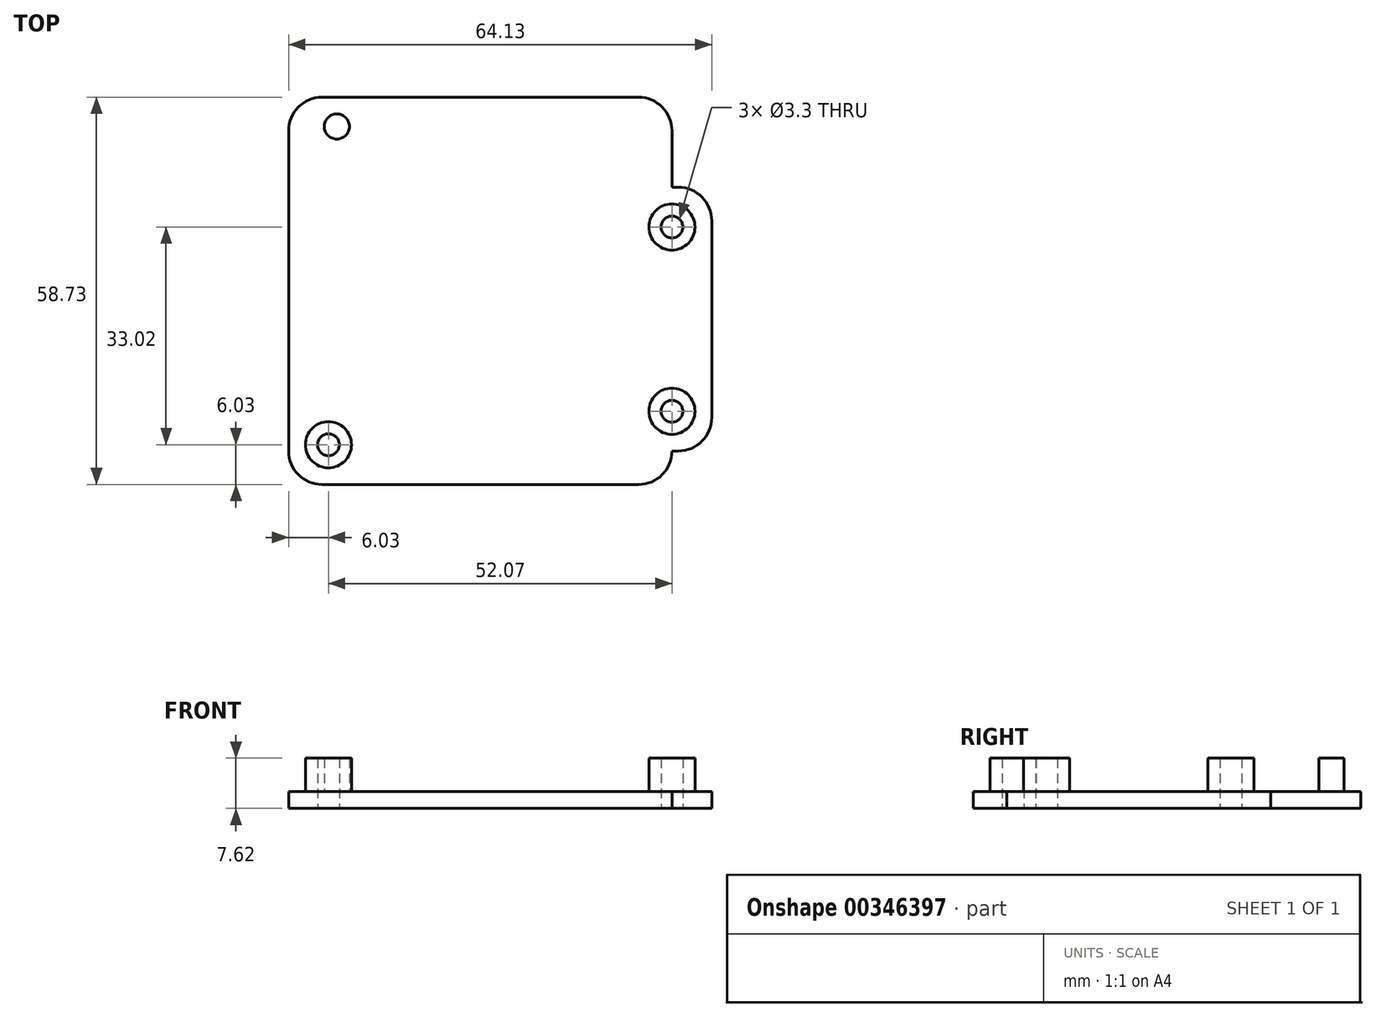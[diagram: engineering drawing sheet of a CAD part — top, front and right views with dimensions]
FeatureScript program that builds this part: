
annotation { "Feature Type Name" : "Feature", "Feature Type Description" : "" }
export const myFeature = defineFeature(function(context is Context, id is Id, definition is map)
    precondition{}
    {
        {
            var Q0;
            Q0=qCreatedBy(makeId("Top.planeOp"),FACE);
            var sketch = newSketch(context, id + "F0", { "sketchPlane" : qUnion([Q0])});
            skPoint(sketch, "E0.middle", {"position": v(0, 0) * mm});
            skLineSegment(sketch, "E1.bottom", {"start": v(25.4, -24.13) * mm, "end": v(-25.4, -24.13) * mm});
            skLineSegment(sketch, "E1.top", {"start": v(25.4, 24.13) * mm, "end": v(-25.4, 24.13) * mm});
            skLineSegment(sketch, "E1.left", {"start": v(25.4, -24.13) * mm, "end": v(25.4, 24.13) * mm});
            skLineSegment(sketch, "E1.right", {"start": v(-25.4, -24.13) * mm, "end": v(-25.4, 24.13) * mm});
            skLineSegment(sketch, "E2", {"start": v(-25.4, 8.9) * mm, "end": v(25.4, 8.9) * mm});
            skLineSegment(sketch, "E3", {"start": v(-25.4, -19.05) * mm, "end": v(25.4, -19.05) * mm});
            skLineSegment(sketch, "E4.bottom", {"start": v(-4.78, -24.13) * mm, "end": v(-26.67, -24.13) * mm});
            skLineSegment(sketch, "E4.top", {"start": v(-4.78, 24.13) * mm, "end": v(-26.67, 24.13) * mm});
            skLineSegment(sketch, "E4.left", {"start": v(-4.78, -24.13) * mm, "end": v(-4.78, 24.13) * mm});
            skLineSegment(sketch, "E4.right", {"start": v(-26.67, -24.13) * mm, "end": v(-26.67, 24.13) * mm});
            skCircle(sketch, "E5", {"center": v(-26.67, -24.13) * mm, "radius": 1.65 * mm});
            skCircle(sketch, "E6", {"center": v(25.4, -19.05) * mm, "radius": 1.65 * mm});
            skCircle(sketch, "E7", {"center": v(25.4, 8.9) * mm, "radius": 1.65 * mm});
            skCircle(sketch, "E8", {"center": v(-26.67, -24.13) * mm, "radius": 3.5 * mm});
            skCircle(sketch, "E9", {"center": v(25.4, -19.05) * mm, "radius": 3.5 * mm});
            skCircle(sketch, "E10", {"center": v(25.4, 8.9) * mm, "radius": 3.5 * mm});
            skCircle(sketch, "E11", {"center": v(-25.4, 24.13) * mm, "radius": 1.9 * mm});
            skSolve(sketch);
        }
        {
            var Q0;
            Q0=qCreatedBy(makeId("Top.planeOp"),FACE);
            var sketch = newSketch(context, id + "F1", { "sketchPlane" : qUnion([Q0])});
            skCircle(sketch, "E12.0", {"center": v(-26.67, -24.13) * mm, "radius": 3.5 * mm});
            skCircle(sketch, "E13.0", {"center": v(-26.67, -24.13) * mm, "radius": 1.65 * mm});
            skCircle(sketch, "E14.0", {"center": v(25.4, -19.05) * mm, "radius": 3.5 * mm});
            skCircle(sketch, "E15.0", {"center": v(25.4, -19.05) * mm, "radius": 1.65 * mm});
            skCircle(sketch, "E16.0", {"center": v(25.4, 8.9) * mm, "radius": 3.5 * mm});
            skCircle(sketch, "E17.0", {"center": v(25.4, 8.9) * mm, "radius": 1.65 * mm});
            skCircle(sketch, "E18.0", {"center": v(-25.4, 24.13) * mm, "radius": 1.9 * mm});
            skLineSegment(sketch, "E19.bottom", {"start": v(32.7, -30.16) * mm, "end": v(-32.7, -30.16) * mm});
            skLineSegment(sketch, "E19.top", {"start": v(32.7, 30.16) * mm, "end": v(-32.7, 30.16) * mm});
            skLineSegment(sketch, "E19.left", {"start": v(32.7, -30.16) * mm, "end": v(32.7, 30.16) * mm});
            skLineSegment(sketch, "E19.right", {"start": v(-32.7, -30.16) * mm, "end": v(-32.7, 30.16) * mm});
            skPoint(sketch, "E19.middle", {"position": v(0, 0) * mm});
            skLineSegment(sketch, "E20", {"start": v(-32.7, 28.57) * mm, "end": v(32.7, 28.57) * mm});
            skLineSegment(sketch, "E21", {"start": v(31.43, 30.16) * mm, "end": v(31.43, -30.16) * mm});
            skLineSegment(sketch, "E22", {"start": v(25.4, -30.16) * mm, "end": v(25.4, 28.58) * mm});
            skLineSegment(sketch, "E23", {"start": v(25.4, 14.92) * mm, "end": v(31.43, 14.92) * mm});
            skLineSegment(sketch, "E24", {"start": v(25.4, -25.08) * mm, "end": v(31.43, -25.08) * mm});
            skSolve(sketch);
        }
        {
            var Q0;
            Q0=makeQuery(id+"F1.imprint","IMPRINT",FACE,{"disambiguationData":[TD([[makeQuery(id+"F1.imprint","IMPRINT",EDGE,{"derivedFrom":sQuery(id+"F1.wireOp",EDGE,"E12.0")}),-1.0]])]});
            var Q1;
            {var subQ0=sQuery(id+"F1.wireOp",EDGE,"E23");Q1=makeQuery(id+"F1.imprint","IMPRINT",FACE,{"disambiguationData":[TD([[makeQuery(id+"F1.imprint","IMPRINT",EDGE,{"derivedFrom":subQ0}),-1.0]])]});}
            extrude(context, id + "F2", {"entities" : qUnion([Q0, Q1]), "depth" : 2.54 * mm, "offsetDistance" : 25.4 * mm});
        }
        {
            var Q0;
            Q0=makeQuery(id+"F1.imprint","IMPRINT",FACE,{"disambiguationData":[TD([[makeQuery(id+"F1.imprint","IMPRINT",EDGE,{"derivedFrom":sQuery(id+"F1.wireOp",EDGE,"E12.0")}),1.0]])]});
            var Q1;
            Q1=makeQuery(id+"F1.imprint","IMPRINT",FACE,{"disambiguationData":[TD([[makeQuery(id+"F1.imprint","IMPRINT",EDGE,{"derivedFrom":sQuery(id+"F1.wireOp",EDGE,"E18.0")}),1.0]])]});
            var Q2;
            {var subQ0=sQuery(id+"F1.wireOp",EDGE,"E22");var subQ1=sQuery(id+"F1.wireOp",EDGE,"E16.0");var subQ2=makeQuery(id+"F1.imprint","INTERSECT",VERTEX,{"disambiguationData":[OD(0.0)],"derivedFrom":[subQ1,subQ0]});Q2=makeQuery(id+"F1.imprint","IMPRINT",FACE,{"disambiguationData":[TD([[makeQuery(id+"F1.imprint","IMPRINT",EDGE,{"disambiguationData":[TD([[subQ2,-1.0]])],"derivedFrom":subQ1}),1.0]])]});}
            var Q3;
            {var subQ0=sQuery(id+"F1.wireOp",EDGE,"E22");var subQ1=sQuery(id+"F1.wireOp",EDGE,"E16.0");var subQ2=makeQuery(id+"F1.imprint","INTERSECT",VERTEX,{"disambiguationData":[OD(0.0)],"derivedFrom":[subQ1,subQ0]});Q3=makeQuery(id+"F1.imprint","IMPRINT",FACE,{"disambiguationData":[TD([[makeQuery(id+"F1.imprint","IMPRINT",EDGE,{"disambiguationData":[TD([[subQ2,1.0]])],"derivedFrom":subQ1}),1.0]])]});}
            var Q4;
            {var subQ0=sQuery(id+"F1.wireOp",EDGE,"E22");var subQ1=sQuery(id+"F1.wireOp",EDGE,"E14.0");var subQ2=makeQuery(id+"F1.imprint","INTERSECT",VERTEX,{"disambiguationData":[OD(0.0)],"derivedFrom":[subQ1,subQ0]});Q4=makeQuery(id+"F1.imprint","IMPRINT",FACE,{"disambiguationData":[TD([[makeQuery(id+"F1.imprint","IMPRINT",EDGE,{"disambiguationData":[TD([[subQ2,-1.0]])],"derivedFrom":subQ1}),1.0]])]});}
            var Q5;
            {var subQ0=sQuery(id+"F1.wireOp",EDGE,"E22");var subQ1=sQuery(id+"F1.wireOp",EDGE,"E14.0");var subQ2=makeQuery(id+"F1.imprint","INTERSECT",VERTEX,{"disambiguationData":[OD(0.0)],"derivedFrom":[subQ1,subQ0]});Q5=makeQuery(id+"F1.imprint","IMPRINT",FACE,{"disambiguationData":[TD([[makeQuery(id+"F1.imprint","IMPRINT",EDGE,{"disambiguationData":[TD([[subQ2,1.0]])],"derivedFrom":subQ1}),1.0]])]});}
            extrude(context, id + "F3", {"entities" : qUnion([Q0, Q1, Q2, Q3, Q4, Q5]), "operationType" : NewBodyOperationType.ADD, "depth" : 7.62 * mm, "offsetDistance" : 25.4 * mm});
        }
        {
            var Q0;
            Q0=makeQuery(id+"F2.opExtrude","SWEPT_EDGE",EDGE,{"disambiguationData":[OSD([sQuery(id+"F1.wireOp",EDGE,"E19.bottom"),sQuery(id+"F1.wireOp",EDGE,"E19.right")])]});
            var Q1;
            Q1=makeQuery(id+"F2.opExtrude","SWEPT_EDGE",EDGE,{"disambiguationData":[OSD([sQuery(id+"F1.wireOp",EDGE,"E19.bottom"),sQuery(id+"F1.wireOp",EDGE,"E22")])]});
            var Q2;
            Q2=makeQuery(id+"F2.opExtrude","SWEPT_EDGE",EDGE,{"disambiguationData":[OSD([sQuery(id+"F1.wireOp",EDGE,"E21"),sQuery(id+"F1.wireOp",EDGE,"E24")])]});
            var Q3;
            Q3=makeQuery(id+"F2.opExtrude","SWEPT_EDGE",EDGE,{"disambiguationData":[OSD([sQuery(id+"F1.wireOp",EDGE,"E21"),sQuery(id+"F1.wireOp",EDGE,"E23")])]});
            var Q4;
            Q4=makeQuery(id+"F2.opExtrude","SWEPT_EDGE",EDGE,{"disambiguationData":[OSD([sQuery(id+"F1.wireOp",EDGE,"E20"),sQuery(id+"F1.wireOp",EDGE,"E22")])]});
            var Q5;
            Q5=makeQuery(id+"F2.opExtrude","SWEPT_EDGE",EDGE,{"disambiguationData":[OSD([sQuery(id+"F1.wireOp",EDGE,"E19.right"),sQuery(id+"F1.wireOp",EDGE,"E20")])]});
            fillet(context, id + "F4", {"entities" : qUnion([Q0, Q1, Q2, Q3, Q4, Q5]), "radius" : 5.08 * mm, "tangentPropagation" : true, "allowEdgeOverflow" : false});
        }
    });
